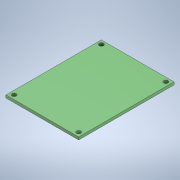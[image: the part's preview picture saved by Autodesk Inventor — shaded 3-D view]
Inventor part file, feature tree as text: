
AUTODESK INVENTOR PART (.ipt)
format: ipt  version: 2022 (Build 260153000, 153)  size: 371,200 bytes
history: native  units: in
note: dims shown in document units (in); Inventor stores cm internally (conversion verified against a paired STEP export)
features: sketch x3, extrude x1, hole x1, emboss x1
ambient origin geometry x8: Origin, YZ Plane, XZ Plane, XY Plane, X Axis, Y Axis, Z Axis, Center Point
bodies: Solid1 (feature_tree)
feature tree (6):
  extrude  "Extrusion1"  Depth=2.2205in
  hole  "Hole1"  [1 undecoded]
  emboss  "Emboss2"
  sketch  "Sketch1"  dims[d0=1.6929in d1=2.2205in]
  sketch  "Sketch2"  dims[d2=0.063in d3=0.0in d4=1.0157in]
  sketch  "Sketch4"  dims[d5=0.752in d6=0.752in d7=1.0157in d8=0.0984in d9=0.75in d10=0.119in d11=0.25in d12=0.5635in d13=1.0in d14=0.8108in d17=0.002in d18=0.0in]
note: 1 required parameter value undecoded (feature->parameter linkage not recoverable at this tier; creation-order binding heuristic only, values carry confidence <= 0.55)
